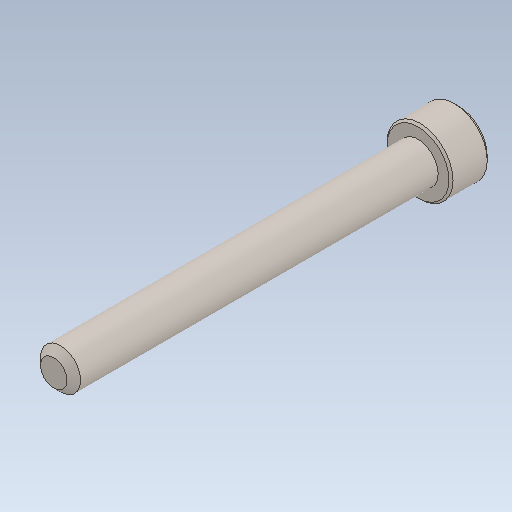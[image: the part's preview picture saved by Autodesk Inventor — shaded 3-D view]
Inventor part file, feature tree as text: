
AUTODESK INVENTOR PART (.ipt)
format: ipt  version: 2020 (Build 240168000, 168)  size: 109,056 bytes
history: native  units: in
note: dims shown in document units (in); Inventor stores cm internally (conversion verified against a paired STEP export)
features: chamfer x1
ambient origin geometry x8: Origin, YZ Plane, XZ Plane, XY Plane, X Axis, Y Axis, Z Axis, Center Point
bodies: Solid1 (feature_tree)
feature tree (1):
  chamfer  "Chamfer2"  [1 undecoded]
note: 1 required parameter value undecoded (feature->parameter linkage not recoverable at this tier; creation-order binding heuristic only, values carry confidence <= 0.55)
